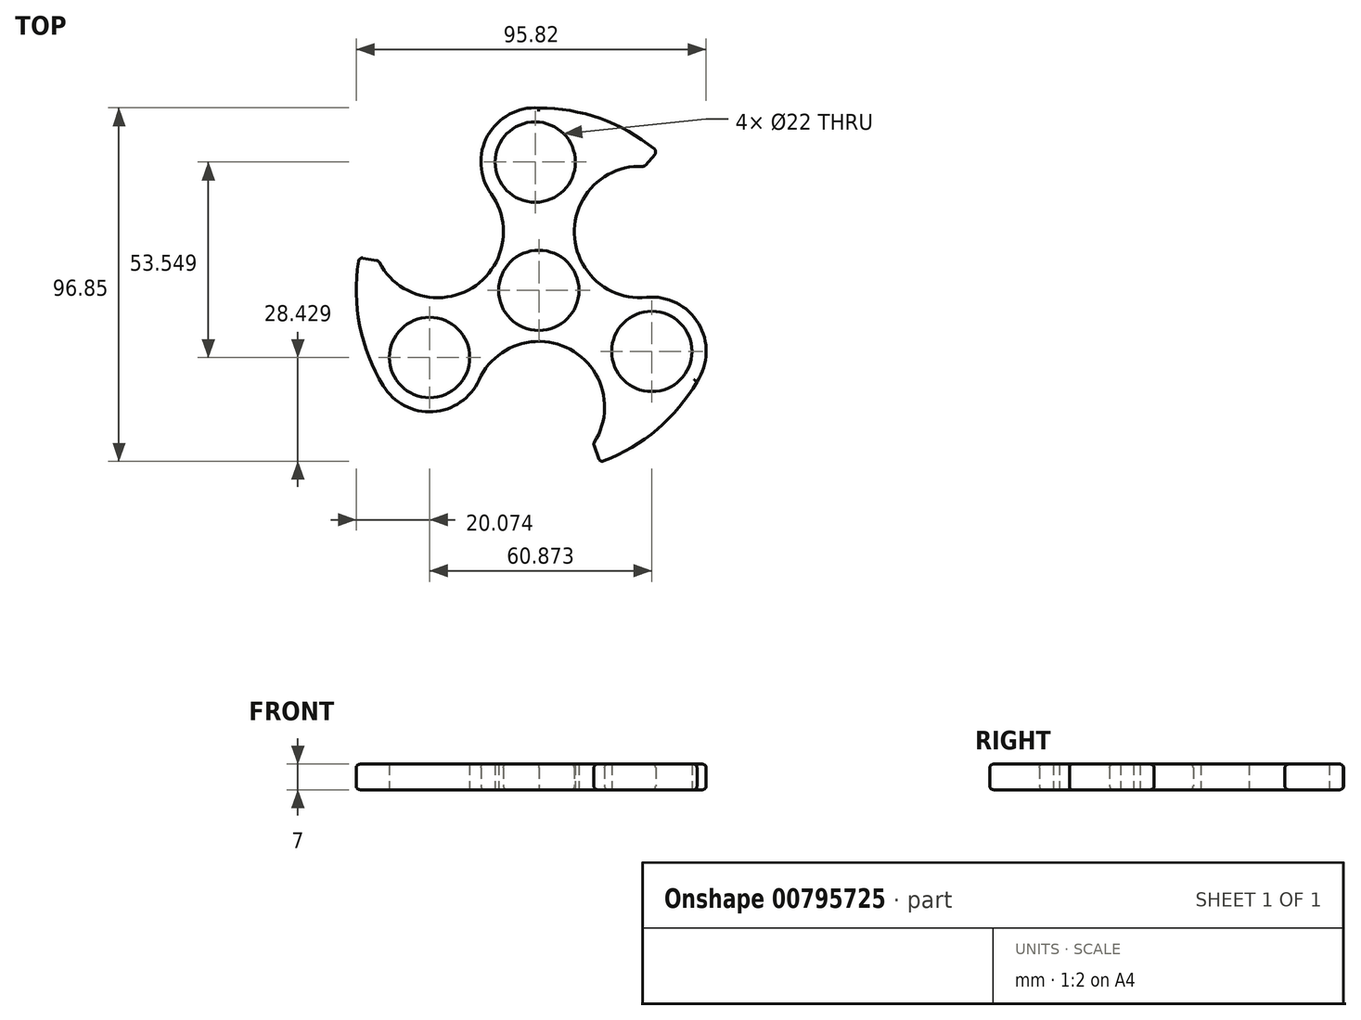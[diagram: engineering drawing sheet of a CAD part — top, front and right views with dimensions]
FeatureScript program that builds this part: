
annotation { "Feature Type Name" : "Feature", "Feature Type Description" : "" }
export const myFeature = defineFeature(function(context is Context, id is Id, definition is map)
    precondition{}
    {
        {
            var Q0;
            Q0=qCreatedBy(makeId("Top.planeOp"),FACE);
            var sketch = newSketch(context, id + "F0", { "sketchPlane" : qUnion([Q0])});
            skCircle(sketch, "E0", {"center": v(0, 0) * mm, "radius": 11 * mm});
            skArc(sketch, "E1", {"start": v(-49.18, 9.03) * mm, "mid": v(-49.15, -9.18) * mm, "end": v(-42.6, -26.18) * mm});
            skArc(sketch, "E2", {"start": v(-43.87, 8.06) * mm, "mid": v(-18.47, 0.56) * mm, "end": v(-13.09, 26.49) * mm});
            skArc(sketch, "E3", {"start": v(28.91, 33.96) * mm, "mid": v(9.72, 15.71) * mm, "end": v(29.48, -1.91) * mm});
            skArc(sketch, "E4", {"start": v(14.95, -42.02) * mm, "mid": v(8.77, -16.28) * mm, "end": v(-16.38, -24.53) * mm});
            skArc(sketch, "E5.trimOffspring", {"start": v(16.76, -47.1) * mm, "mid": v(32, -38.42) * mm, "end": v(43.3, -25) * mm});
            skArc(sketch, "E6.trimOffspring", {"start": v(32.41, 38.07) * mm, "mid": v(17.27, 46.92) * mm, "end": v(0, 50) * mm});
            skPoint(sketch, "E7", {"position": v(23.2, 38.55) * mm});
            skPoint(sketch, "E8", {"position": v(21.79, -39.38) * mm});
            skPoint(sketch, "E9", {"position": v(-45, 0.82) * mm});
            skArc(sketch, "E10", {"start": v(-13.09, 26.49) * mm, "mid": v(-14, 42.4) * mm, "end": v(0, 50) * mm});
            skArc(sketch, "E11", {"start": v(-42.6, -26.18) * mm, "mid": v(-29, -33.24) * mm, "end": v(-16.38, -24.53) * mm});
            skArc(sketch, "E12", {"start": v(29.48, -1.91) * mm, "mid": v(43.71, -9.08) * mm, "end": v(43.3, -25) * mm});
            skCircle(sketch, "E13", {"center": v(-29.93, -18.4) * mm, "radius": 11 * mm});
            skCircle(sketch, "E14", {"center": v(-1, 35.16) * mm, "radius": 11 * mm});
            skCircle(sketch, "E15", {"center": v(30.95, -16.72) * mm, "radius": 11 * mm});
            skLineSegment(sketch, "E16", {"start": v(0, 0) * mm, "end": v(37.87, 44.49) * mm, "construction": true});
            skLineSegment(sketch, "E17.1.0", {"start": v(0, 0) * mm, "end": v(-57.46, 10.56) * mm, "construction": true});
            skLineSegment(sketch, "E17.2.0", {"start": v(0, 0) * mm, "end": v(19.59, -55.04) * mm, "construction": true});
            skLineSegment(sketch, "E18", {"start": v(-49.18, 9.03) * mm, "end": v(-43.87, 8.06) * mm});
            skLineSegment(sketch, "E19", {"start": v(14.95, -42.02) * mm, "end": v(16.76, -47.1) * mm});
            skLineSegment(sketch, "E20", {"start": v(32.41, 38.07) * mm, "end": v(28.91, 33.96) * mm});
            skSolve(sketch);
        }
        {
            var Q0;
            {var subQ1=sQuery(id+"F0.wireOp",EDGE,"3f7bc842-8467-49ac-8440-9adaad4e2810.2");Q0=makeQuery(id+"F0.imprint","IMPRINT",FACE,{"disambiguationData":[TD([[makeQuery(id+"F0.imprint","IMPRINT",EDGE,{"derivedFrom":subQ1}),1.0]])]});}
            var Q1;
            {var subQ5=sQuery(id+"F0.wireOp",EDGE,"3f7bc842-8467-49ac-8440-9adaad4e2810.0");Q1=makeQuery(id+"F0.imprint","IMPRINT",FACE,{"disambiguationData":[TD([[makeQuery(id+"F0.imprint","IMPRINT",EDGE,{"derivedFrom":subQ5}),1.0]])]});}
            var Q2;
            {var subQ0=sQuery(id+"F0.wireOp",EDGE,"3f7bc842-8467-49ac-8440-9adaad4e2810.1");var subQ1=sQuery(id+"F0.wireOp",EDGE,"nu7MbhjY-MAc7-rPjX-g1DX-lD3kLk05fhsn");var subQ2=makeQuery(id+"F0.imprint","INTERSECT",VERTEX,{"derivedFrom":[subQ1,subQ0]});Q2=makeQuery(id+"F0.imprint","IMPRINT",FACE,{"disambiguationData":[TD([[makeQuery(id+"F0.imprint","IMPRINT",EDGE,{"disambiguationData":[TD([[subQ2,1.0]])],"derivedFrom":subQ0}),1.0]])]});}
            var Q3;
            {var subQ0=sQuery(id+"F0.wireOp",EDGE,"3f7bc842-8467-49ac-8440-9adaad4e2810.1");var subQ1=sQuery(id+"F0.wireOp",EDGE,"nu7MbhjY-MAc7-rPjX-g1DX-lD3kLk05fhsn");var subQ2=makeQuery(id+"F0.imprint","INTERSECT",VERTEX,{"derivedFrom":[subQ1,subQ0]});Q3=makeQuery(id+"F0.imprint","IMPRINT",FACE,{"disambiguationData":[TD([[makeQuery(id+"F0.imprint","IMPRINT",EDGE,{"disambiguationData":[TD([[subQ2,-1.0]])],"derivedFrom":subQ0}),1.0]])]});}
            var Q4;
            {var subQ0=sQuery(id+"F0.wireOp",EDGE,"E2");var subQ1=sQuery(id+"F0.wireOp",EDGE,"sv7fbsnc-qcye-DYNE-iSqw-857IQjWxAevf");var subQ2=makeQuery(id+"F0.imprint","INTERSECT",VERTEX,{"derivedFrom":[subQ1,subQ0]});Q4=makeQuery(id+"F0.imprint","IMPRINT",FACE,{"disambiguationData":[TD([[makeQuery(id+"F0.imprint","IMPRINT",EDGE,{"disambiguationData":[TD([[subQ2,-1.0]])],"derivedFrom":subQ1}),-1.0]])]});}
            var Q5;
            {var subQ0=sQuery(id+"F0.wireOp",EDGE,"E3");var subQ1=sQuery(id+"F0.wireOp",EDGE,"sv7fbsnc-qcye-DYNE-iSqw-857IQjWxAevf");var subQ2=makeQuery(id+"F0.imprint","INTERSECT",VERTEX,{"derivedFrom":[subQ1,subQ0]});Q5=makeQuery(id+"F0.imprint","IMPRINT",FACE,{"disambiguationData":[TD([[makeQuery(id+"F0.imprint","IMPRINT",EDGE,{"disambiguationData":[TD([[subQ2,1.0]])],"derivedFrom":subQ1}),-1.0]])]});}
            var Q6;
            {var subQ3=sQuery(id+"F0.wireOp",EDGE,"E2");var subQ5=sQuery(id+"F0.wireOp",EDGE,"C4j8nSnC-YMSu-Lszk-EYxg-b8w5SDZCJpY5");var subQ6=makeQuery(id+"F0.imprint","INTERSECT",VERTEX,{"disambiguationData":[OD(0.0)],"derivedFrom":[subQ5,subQ3]});Q6=makeQuery(id+"F0.imprint","IMPRINT",FACE,{"disambiguationData":[TD([[makeQuery(id+"F0.imprint","IMPRINT",EDGE,{"disambiguationData":[TD([[subQ6,1.0]])],"derivedFrom":subQ5}),1.0]])]});}
            var Q7;
            {var subQ1=sQuery(id+"F0.wireOp",EDGE,"C4j8nSnC-YMSu-Lszk-EYxg-b8w5SDZCJpY5");var subQ7=sQuery(id+"F0.wireOp",EDGE,"E3");var subQ9=makeQuery(id+"F0.imprint","INTERSECT",VERTEX,{"disambiguationData":[OD(1.0)],"derivedFrom":[subQ1,subQ7]});Q7=makeQuery(id+"F0.imprint","IMPRINT",FACE,{"disambiguationData":[TD([[makeQuery(id+"F0.imprint","IMPRINT",EDGE,{"disambiguationData":[TD([[subQ9,-1.0]])],"derivedFrom":subQ1}),1.0]])]});}
            var Q8;
            {var subQ1=sQuery(id+"F0.wireOp",EDGE,"C4j8nSnC-YMSu-Lszk-EYxg-b8w5SDZCJpY5");var subQ5=sQuery(id+"F0.wireOp",EDGE,"E2");var subQ6=makeQuery(id+"F0.imprint","INTERSECT",VERTEX,{"disambiguationData":[OD(1.0)],"derivedFrom":[subQ1,subQ5]});Q8=makeQuery(id+"F0.imprint","IMPRINT",FACE,{"disambiguationData":[TD([[makeQuery(id+"F0.imprint","IMPRINT",EDGE,{"disambiguationData":[TD([[subQ6,-1.0]])],"derivedFrom":subQ1}),1.0]])]});}
            var Q9;
            {var subQ1=sQuery(id+"F0.wireOp",EDGE,"C4j8nSnC-YMSu-Lszk-EYxg-b8w5SDZCJpY5");var subQ5=sQuery(id+"F0.wireOp",EDGE,"E4");var subQ6=makeQuery(id+"F0.imprint","INTERSECT",VERTEX,{"disambiguationData":[OD(0.0)],"derivedFrom":[subQ1,subQ5]});Q9=makeQuery(id+"F0.imprint","IMPRINT",FACE,{"disambiguationData":[TD([[makeQuery(id+"F0.imprint","IMPRINT",EDGE,{"disambiguationData":[TD([[subQ6,1.0]])],"derivedFrom":subQ1}),1.0]])]});}
            var Q10;
            {var subQ5=sQuery(id+"F0.wireOp",EDGE,"9VgUR1kC-HbJB-ABtG-h0EX-FUHrEpssJFZg");var subQ6=sQuery(id+"F0.wireOp",EDGE,"E0");var subQ7=makeQuery(id+"F0.imprint","INTERSECT",VERTEX,{"derivedFrom":[subQ6,subQ5]});Q10=makeQuery(id+"F0.imprint","IMPRINT",FACE,{"disambiguationData":[TD([[makeQuery(id+"F0.imprint","IMPRINT",EDGE,{"disambiguationData":[TD([[subQ7,-1.0]])],"derivedFrom":subQ6}),-1.0]])]});}
            var Q11;
            {var subQ1=sQuery(id+"F0.wireOp",EDGE,"E0");var subQ9=sQuery(id+"F0.wireOp",EDGE,"CFaMabJv-BaBl-nt57-wO3A-6JOnLyDZJUd2");var subQ11=makeQuery(id+"F0.imprint","INTERSECT",VERTEX,{"derivedFrom":[subQ1,subQ9]});Q11=makeQuery(id+"F0.imprint","IMPRINT",FACE,{"disambiguationData":[TD([[makeQuery(id+"F0.imprint","IMPRINT",EDGE,{"disambiguationData":[TD([[subQ11,1.0]])],"derivedFrom":subQ1}),-1.0]])]});}
            var Q12;
            {var subQ0=sQuery(id+"F0.wireOp",EDGE,"E3");var subQ1=sQuery(id+"F0.wireOp",EDGE,"x40MpVTq-PCuQ-1TBw-DNN8-5xuqoy8G5yz2");var subQ2=makeQuery(id+"F0.imprint","INTERSECT",VERTEX,{"derivedFrom":[subQ1,subQ0]});Q12=makeQuery(id+"F0.imprint","IMPRINT",FACE,{"disambiguationData":[TD([[makeQuery(id+"F0.imprint","IMPRINT",EDGE,{"disambiguationData":[TD([[subQ2,-1.0]])],"derivedFrom":subQ1}),-1.0]])]});}
            var Q13;
            {var subQ0=sQuery(id+"F0.wireOp",EDGE,"E4");var subQ1=sQuery(id+"F0.wireOp",EDGE,"x40MpVTq-PCuQ-1TBw-DNN8-5xuqoy8G5yz2");var subQ2=makeQuery(id+"F0.imprint","INTERSECT",VERTEX,{"derivedFrom":[subQ1,subQ0]});Q13=makeQuery(id+"F0.imprint","IMPRINT",FACE,{"disambiguationData":[TD([[makeQuery(id+"F0.imprint","IMPRINT",EDGE,{"disambiguationData":[TD([[subQ2,1.0]])],"derivedFrom":subQ1}),-1.0]])]});}
            var Q14;
            {var subQ0=sQuery(id+"F0.wireOp",EDGE,"49722dc7-dc7b-4ebf-b22a-0d9910023828.2");Q14=makeQuery(id+"F0.imprint","IMPRINT",FACE,{"disambiguationData":[TD([[makeQuery(id+"F0.imprint","IMPRINT",EDGE,{"derivedFrom":subQ0}),1.0]])]});}
            var Q15;
            {var subQ5=sQuery(id+"F0.wireOp",EDGE,"49722dc7-dc7b-4ebf-b22a-0d9910023828.0");Q15=makeQuery(id+"F0.imprint","IMPRINT",FACE,{"disambiguationData":[TD([[makeQuery(id+"F0.imprint","IMPRINT",EDGE,{"derivedFrom":subQ5}),1.0]])]});}
            var Q16;
            {var subQ0=sQuery(id+"F0.wireOp",EDGE,"E5.trimOffspring");Q16=makeQuery(id+"F0.imprint","IMPRINT",FACE,{"disambiguationData":[TD([[makeQuery(id+"F0.imprint","IMPRINT",EDGE,{"derivedFrom":subQ0}),1.0]])]});}
            var Q17;
            {var subQ0=sQuery(id+"F0.wireOp",EDGE,"49722dc7-dc7b-4ebf-b22a-0d9910023828.4");var subQ1=sQuery(id+"F0.wireOp",EDGE,"88UstpRX-54K3-uVYN-JsYc-c1O7LK7eOc8f");var subQ2=makeQuery(id+"F0.imprint","INTERSECT",VERTEX,{"derivedFrom":[subQ1,subQ0]});Q17=makeQuery(id+"F0.imprint","IMPRINT",FACE,{"disambiguationData":[TD([[makeQuery(id+"F0.imprint","IMPRINT",EDGE,{"disambiguationData":[TD([[subQ2,1.0]])],"derivedFrom":subQ0}),1.0]])]});}
            var Q18;
            {var subQ0=sQuery(id+"F0.wireOp",EDGE,"49722dc7-dc7b-4ebf-b22a-0d9910023828.4");var subQ1=sQuery(id+"F0.wireOp",EDGE,"88UstpRX-54K3-uVYN-JsYc-c1O7LK7eOc8f");var subQ2=makeQuery(id+"F0.imprint","INTERSECT",VERTEX,{"derivedFrom":[subQ1,subQ0]});Q18=makeQuery(id+"F0.imprint","IMPRINT",FACE,{"disambiguationData":[TD([[makeQuery(id+"F0.imprint","IMPRINT",EDGE,{"disambiguationData":[TD([[subQ2,-1.0]])],"derivedFrom":subQ0}),1.0]])]});}
            var Q19;
            {var subQ0=sQuery(id+"F0.wireOp",EDGE,"E6.trimOffspring");Q19=makeQuery(id+"F0.imprint","IMPRINT",FACE,{"disambiguationData":[TD([[makeQuery(id+"F0.imprint","IMPRINT",EDGE,{"derivedFrom":subQ0}),1.0]])]});}
            var Q20;
            {var subQ0=sQuery(id+"F0.wireOp",EDGE,"4Rxz6dJ8-GsAv-ijvN-txGC-AziJ4LwzvlZd");var subQ1=sQuery(id+"F0.wireOp",EDGE,"sv7fbsnc-qcye-DYNE-iSqw-857IQjWxAevf");var subQ2=makeQuery(id+"F0.imprint","INTERSECT",VERTEX,{"disambiguationData":[OD(0.0)],"derivedFrom":[subQ1,subQ0]});Q20=makeQuery(id+"F0.imprint","IMPRINT",FACE,{"disambiguationData":[TD([[makeQuery(id+"F0.imprint","IMPRINT",EDGE,{"disambiguationData":[TD([[subQ2,-1.0]])],"derivedFrom":subQ0}),1.0]])]});}
            var Q21;
            {var subQ0=sQuery(id+"F0.wireOp",EDGE,"4Rxz6dJ8-GsAv-ijvN-txGC-AziJ4LwzvlZd");var subQ1=sQuery(id+"F0.wireOp",EDGE,"sv7fbsnc-qcye-DYNE-iSqw-857IQjWxAevf");var subQ2=makeQuery(id+"F0.imprint","INTERSECT",VERTEX,{"disambiguationData":[OD(1.0)],"derivedFrom":[subQ1,subQ0]});Q21=makeQuery(id+"F0.imprint","IMPRINT",FACE,{"disambiguationData":[TD([[makeQuery(id+"F0.imprint","IMPRINT",EDGE,{"disambiguationData":[TD([[subQ2,1.0]])],"derivedFrom":subQ0}),1.0]])]});}
            var Q22;
            {var subQ0=sQuery(id+"F0.wireOp",EDGE,"4Rxz6dJ8-GsAv-ijvN-txGC-AziJ4LwzvlZd");var subQ3=sQuery(id+"F0.wireOp",EDGE,"C4j8nSnC-YMSu-Lszk-EYxg-b8w5SDZCJpY5");var subQ5=makeQuery(id+"F0.imprint","INTERSECT",VERTEX,{"disambiguationData":[OD(0.0)],"derivedFrom":[subQ3,subQ0]});Q22=makeQuery(id+"F0.imprint","IMPRINT",FACE,{"disambiguationData":[TD([[makeQuery(id+"F0.imprint","IMPRINT",EDGE,{"disambiguationData":[TD([[subQ5,-1.0]])],"derivedFrom":subQ3}),1.0]])]});}
            var Q23;
            {var subQ0=sQuery(id+"F0.wireOp",EDGE,"4Rxz6dJ8-GsAv-ijvN-txGC-AziJ4LwzvlZd");var subQ3=sQuery(id+"F0.wireOp",EDGE,"C4j8nSnC-YMSu-Lszk-EYxg-b8w5SDZCJpY5");var subQ5=makeQuery(id+"F0.imprint","INTERSECT",VERTEX,{"disambiguationData":[OD(1.0)],"derivedFrom":[subQ3,subQ0]});Q23=makeQuery(id+"F0.imprint","IMPRINT",FACE,{"disambiguationData":[TD([[makeQuery(id+"F0.imprint","IMPRINT",EDGE,{"disambiguationData":[TD([[subQ5,1.0]])],"derivedFrom":subQ3}),1.0]])]});}
            var Q24;
            {var subQ0=sQuery(id+"F0.wireOp",EDGE,"gMAYUmRH-FaYY-2lfT-oHka-ojM136KSUSHD");var subQ1=sQuery(id+"F0.wireOp",EDGE,"88UstpRX-54K3-uVYN-JsYc-c1O7LK7eOc8f");var subQ2=makeQuery(id+"F0.imprint","INTERSECT",VERTEX,{"disambiguationData":[OD(0.0)],"derivedFrom":[subQ1,subQ0]});Q24=makeQuery(id+"F0.imprint","IMPRINT",FACE,{"disambiguationData":[TD([[makeQuery(id+"F0.imprint","IMPRINT",EDGE,{"disambiguationData":[TD([[subQ2,-1.0]])],"derivedFrom":subQ1}),1.0]])]});}
            var Q25;
            {var subQ0=sQuery(id+"F0.wireOp",EDGE,"gMAYUmRH-FaYY-2lfT-oHka-ojM136KSUSHD");var subQ1=sQuery(id+"F0.wireOp",EDGE,"88UstpRX-54K3-uVYN-JsYc-c1O7LK7eOc8f");var subQ2=makeQuery(id+"F0.imprint","INTERSECT",VERTEX,{"disambiguationData":[OD(0.0)],"derivedFrom":[subQ1,subQ0]});Q25=makeQuery(id+"F0.imprint","IMPRINT",FACE,{"disambiguationData":[TD([[makeQuery(id+"F0.imprint","IMPRINT",EDGE,{"disambiguationData":[TD([[subQ2,-1.0]])],"derivedFrom":subQ1}),-1.0]])]});}
            var Q26;
            {var subQ1=sQuery(id+"F0.wireOp",EDGE,"88UstpRX-54K3-uVYN-JsYc-c1O7LK7eOc8f");var subQ5=sQuery(id+"F0.wireOp",EDGE,"C4j8nSnC-YMSu-Lszk-EYxg-b8w5SDZCJpY5");var subQ6=makeQuery(id+"F0.imprint","INTERSECT",VERTEX,{"derivedFrom":[subQ1,subQ5]});Q26=makeQuery(id+"F0.imprint","IMPRINT",FACE,{"disambiguationData":[TD([[makeQuery(id+"F0.imprint","IMPRINT",EDGE,{"disambiguationData":[TD([[subQ6,-1.0]])],"derivedFrom":subQ1}),-1.0]])]});}
            var Q27;
            {var subQ1=sQuery(id+"F0.wireOp",EDGE,"88UstpRX-54K3-uVYN-JsYc-c1O7LK7eOc8f");var subQ7=sQuery(id+"F0.wireOp",EDGE,"C4j8nSnC-YMSu-Lszk-EYxg-b8w5SDZCJpY5");var subQ8=makeQuery(id+"F0.imprint","INTERSECT",VERTEX,{"derivedFrom":[subQ1,subQ7]});Q27=makeQuery(id+"F0.imprint","IMPRINT",FACE,{"disambiguationData":[TD([[makeQuery(id+"F0.imprint","IMPRINT",EDGE,{"disambiguationData":[TD([[subQ8,-1.0]])],"derivedFrom":subQ1}),1.0]])]});}
            var Q28;
            {var subQ0=sQuery(id+"F0.wireOp",EDGE,"E1");Q28=makeQuery(id+"F0.imprint","IMPRINT",FACE,{"disambiguationData":[TD([[makeQuery(id+"F0.imprint","IMPRINT",EDGE,{"derivedFrom":subQ0}),1.0]])]});}
            var Q29;
            {var subQ1=sQuery(id+"F0.wireOp",EDGE,"d8093a5b-4d6d-4e08-b9a8-8a5bac8dbfa5.3");Q29=makeQuery(id+"F0.imprint","IMPRINT",FACE,{"disambiguationData":[TD([[makeQuery(id+"F0.imprint","IMPRINT",EDGE,{"derivedFrom":subQ1}),1.0]])]});}
            var Q30;
            {var subQ4=sQuery(id+"F0.wireOp",EDGE,"d8093a5b-4d6d-4e08-b9a8-8a5bac8dbfa5.0");Q30=makeQuery(id+"F0.imprint","IMPRINT",FACE,{"disambiguationData":[TD([[makeQuery(id+"F0.imprint","IMPRINT",EDGE,{"derivedFrom":subQ4}),1.0]])]});}
            var Q31;
            {var subQ0=sQuery(id+"F0.wireOp",EDGE,"E4");var subQ1=sQuery(id+"F0.wireOp",EDGE,"RUABtInU-iKBV-EQpS-h9ne-nRwwB5inRPBh");var subQ2=makeQuery(id+"F0.imprint","INTERSECT",VERTEX,{"derivedFrom":[subQ1,subQ0]});Q31=makeQuery(id+"F0.imprint","IMPRINT",FACE,{"disambiguationData":[TD([[makeQuery(id+"F0.imprint","IMPRINT",EDGE,{"disambiguationData":[TD([[subQ2,-1.0]])],"derivedFrom":subQ1}),-1.0]])]});}
            var Q32;
            {var subQ0=sQuery(id+"F0.wireOp",EDGE,"E2");var subQ1=sQuery(id+"F0.wireOp",EDGE,"RUABtInU-iKBV-EQpS-h9ne-nRwwB5inRPBh");var subQ2=makeQuery(id+"F0.imprint","INTERSECT",VERTEX,{"derivedFrom":[subQ1,subQ0]});Q32=makeQuery(id+"F0.imprint","IMPRINT",FACE,{"disambiguationData":[TD([[makeQuery(id+"F0.imprint","IMPRINT",EDGE,{"disambiguationData":[TD([[subQ2,1.0]])],"derivedFrom":subQ1}),-1.0]])]});}
            var Q33;
            {var subQ0=sQuery(id+"F0.wireOp",EDGE,"d8093a5b-4d6d-4e08-b9a8-8a5bac8dbfa5.5");var subQ1=sQuery(id+"F0.wireOp",EDGE,"mKOXe6AH-uMiB-TUgd-KZ6j-uo9zpwvRpa4S");var subQ2=makeQuery(id+"F0.imprint","INTERSECT",VERTEX,{"derivedFrom":[subQ1,subQ0]});Q33=makeQuery(id+"F0.imprint","IMPRINT",FACE,{"disambiguationData":[TD([[makeQuery(id+"F0.imprint","IMPRINT",EDGE,{"disambiguationData":[TD([[subQ2,-1.0]])],"derivedFrom":subQ0}),1.0]])]});}
            var Q34;
            {var subQ0=sQuery(id+"F0.wireOp",EDGE,"d8093a5b-4d6d-4e08-b9a8-8a5bac8dbfa5.5");var subQ1=sQuery(id+"F0.wireOp",EDGE,"mKOXe6AH-uMiB-TUgd-KZ6j-uo9zpwvRpa4S");var subQ2=makeQuery(id+"F0.imprint","INTERSECT",VERTEX,{"derivedFrom":[subQ1,subQ0]});Q34=makeQuery(id+"F0.imprint","IMPRINT",FACE,{"disambiguationData":[TD([[makeQuery(id+"F0.imprint","IMPRINT",EDGE,{"disambiguationData":[TD([[subQ2,1.0]])],"derivedFrom":subQ0}),1.0]])]});}
            var Q35;
            {var subQ0=sQuery(id+"F0.wireOp",EDGE,"kEFfzBxr-I8kb-SGwx-hxRS-iwMc0eVOOg4E");var subQ1=sQuery(id+"F0.wireOp",EDGE,"RUABtInU-iKBV-EQpS-h9ne-nRwwB5inRPBh");var subQ2=makeQuery(id+"F0.imprint","INTERSECT",VERTEX,{"disambiguationData":[OD(1.0)],"derivedFrom":[subQ1,subQ0]});Q35=makeQuery(id+"F0.imprint","IMPRINT",FACE,{"disambiguationData":[TD([[makeQuery(id+"F0.imprint","IMPRINT",EDGE,{"disambiguationData":[TD([[subQ2,1.0]])],"derivedFrom":subQ0}),1.0]])]});}
            var Q36;
            {var subQ0=sQuery(id+"F0.wireOp",EDGE,"kEFfzBxr-I8kb-SGwx-hxRS-iwMc0eVOOg4E");var subQ1=sQuery(id+"F0.wireOp",EDGE,"RUABtInU-iKBV-EQpS-h9ne-nRwwB5inRPBh");var subQ2=makeQuery(id+"F0.imprint","INTERSECT",VERTEX,{"disambiguationData":[OD(0.0)],"derivedFrom":[subQ1,subQ0]});Q36=makeQuery(id+"F0.imprint","IMPRINT",FACE,{"disambiguationData":[TD([[makeQuery(id+"F0.imprint","IMPRINT",EDGE,{"disambiguationData":[TD([[subQ2,-1.0]])],"derivedFrom":subQ0}),1.0]])]});}
            var Q37;
            {var subQ0=sQuery(id+"F0.wireOp",EDGE,"kEFfzBxr-I8kb-SGwx-hxRS-iwMc0eVOOg4E");var subQ3=sQuery(id+"F0.wireOp",EDGE,"C4j8nSnC-YMSu-Lszk-EYxg-b8w5SDZCJpY5");var subQ5=makeQuery(id+"F0.imprint","INTERSECT",VERTEX,{"disambiguationData":[OD(1.0)],"derivedFrom":[subQ3,subQ0]});Q37=makeQuery(id+"F0.imprint","IMPRINT",FACE,{"disambiguationData":[TD([[makeQuery(id+"F0.imprint","IMPRINT",EDGE,{"disambiguationData":[TD([[subQ5,1.0]])],"derivedFrom":subQ3}),1.0]])]});}
            var Q38;
            {var subQ0=sQuery(id+"F0.wireOp",EDGE,"kEFfzBxr-I8kb-SGwx-hxRS-iwMc0eVOOg4E");var subQ3=sQuery(id+"F0.wireOp",EDGE,"C4j8nSnC-YMSu-Lszk-EYxg-b8w5SDZCJpY5");var subQ5=makeQuery(id+"F0.imprint","INTERSECT",VERTEX,{"disambiguationData":[OD(0.0)],"derivedFrom":[subQ3,subQ0]});Q38=makeQuery(id+"F0.imprint","IMPRINT",FACE,{"disambiguationData":[TD([[makeQuery(id+"F0.imprint","IMPRINT",EDGE,{"disambiguationData":[TD([[subQ5,-1.0]])],"derivedFrom":subQ3}),1.0]])]});}
            var Q39;
            {var subQ0=sQuery(id+"F0.wireOp",EDGE,"DQ5kVecW-1MrT-lyVf-wv95-HuLgpyEHOht9");var subQ1=sQuery(id+"F0.wireOp",EDGE,"C4j8nSnC-YMSu-Lszk-EYxg-b8w5SDZCJpY5");var subQ2=makeQuery(id+"F0.imprint","INTERSECT",VERTEX,{"derivedFrom":[subQ1,subQ0]});Q39=makeQuery(id+"F0.imprint","IMPRINT",FACE,{"disambiguationData":[TD([[makeQuery(id+"F0.imprint","IMPRINT",EDGE,{"disambiguationData":[TD([[subQ2,-1.0]])],"derivedFrom":subQ1}),1.0]])]});}
            var Q40;
            {var subQ0=sQuery(id+"F0.wireOp",EDGE,"DQ5kVecW-1MrT-lyVf-wv95-HuLgpyEHOht9");var subQ1=sQuery(id+"F0.wireOp",EDGE,"C4j8nSnC-YMSu-Lszk-EYxg-b8w5SDZCJpY5");var subQ2=makeQuery(id+"F0.imprint","INTERSECT",VERTEX,{"derivedFrom":[subQ1,subQ0]});Q40=makeQuery(id+"F0.imprint","IMPRINT",FACE,{"disambiguationData":[TD([[makeQuery(id+"F0.imprint","IMPRINT",EDGE,{"disambiguationData":[TD([[subQ2,1.0]])],"derivedFrom":subQ1}),1.0]])]});}
            var Q41;
            {var subQ0=sQuery(id+"F0.wireOp",EDGE,"CFaMabJv-BaBl-nt57-wO3A-6JOnLyDZJUd2");var subQ1=sQuery(id+"F0.wireOp",EDGE,"C4j8nSnC-YMSu-Lszk-EYxg-b8w5SDZCJpY5");var subQ2=makeQuery(id+"F0.imprint","INTERSECT",VERTEX,{"derivedFrom":[subQ1,subQ0]});Q41=makeQuery(id+"F0.imprint","IMPRINT",FACE,{"disambiguationData":[TD([[makeQuery(id+"F0.imprint","IMPRINT",EDGE,{"disambiguationData":[TD([[subQ2,-1.0]])],"derivedFrom":subQ1}),1.0]])]});}
            var Q42;
            {var subQ0=sQuery(id+"F0.wireOp",EDGE,"CFaMabJv-BaBl-nt57-wO3A-6JOnLyDZJUd2");var subQ1=sQuery(id+"F0.wireOp",EDGE,"C4j8nSnC-YMSu-Lszk-EYxg-b8w5SDZCJpY5");var subQ2=makeQuery(id+"F0.imprint","INTERSECT",VERTEX,{"derivedFrom":[subQ1,subQ0]});Q42=makeQuery(id+"F0.imprint","IMPRINT",FACE,{"disambiguationData":[TD([[makeQuery(id+"F0.imprint","IMPRINT",EDGE,{"disambiguationData":[TD([[subQ2,1.0]])],"derivedFrom":subQ1}),1.0]])]});}
            var Q43;
            {var subQ0=sQuery(id+"F0.wireOp",EDGE,"9VgUR1kC-HbJB-ABtG-h0EX-FUHrEpssJFZg");var subQ1=sQuery(id+"F0.wireOp",EDGE,"C4j8nSnC-YMSu-Lszk-EYxg-b8w5SDZCJpY5");var subQ2=makeQuery(id+"F0.imprint","INTERSECT",VERTEX,{"derivedFrom":[subQ1,subQ0]});Q43=makeQuery(id+"F0.imprint","IMPRINT",FACE,{"disambiguationData":[TD([[makeQuery(id+"F0.imprint","IMPRINT",EDGE,{"disambiguationData":[TD([[subQ2,-1.0]])],"derivedFrom":subQ1}),1.0]])]});}
            var Q44;
            {var subQ0=sQuery(id+"F0.wireOp",EDGE,"9VgUR1kC-HbJB-ABtG-h0EX-FUHrEpssJFZg");var subQ1=sQuery(id+"F0.wireOp",EDGE,"C4j8nSnC-YMSu-Lszk-EYxg-b8w5SDZCJpY5");var subQ2=makeQuery(id+"F0.imprint","INTERSECT",VERTEX,{"derivedFrom":[subQ1,subQ0]});Q44=makeQuery(id+"F0.imprint","IMPRINT",FACE,{"disambiguationData":[TD([[makeQuery(id+"F0.imprint","IMPRINT",EDGE,{"disambiguationData":[TD([[subQ2,1.0]])],"derivedFrom":subQ1}),1.0]])]});}
            extrude(context, id + "F1", {"entities" : qUnion([Q0, Q1, Q2, Q3, Q4, Q5, Q6, Q7, Q8, Q9, Q10, Q11, Q12, Q13, Q14, Q15, Q16, Q17, Q18, Q19, Q20, Q21, Q22, Q23, Q24, Q25, Q26, Q27, Q28, Q29, Q30, Q31, Q32, Q33, Q34, Q35, Q36, Q37, Q38, Q39, Q40, Q41, Q42, Q43, Q44]), "depth" : 7 * mm, "offsetDistance" : 25 * mm});
        }
        {
            var Q0;
            Q0=makeQuery(id+"F1.opExtrude","CAP_EDGE",EDGE,{"disambiguationData":[OSD([sQuery(id+"F0.wireOp",EDGE,"E2")])],"isStart":false});
            var Q1;
            Q1=makeQuery(id+"F1.opExtrude","CAP_EDGE",EDGE,{"disambiguationData":[OSD([sQuery(id+"F0.wireOp",EDGE,"E4")])],"isStart":false});
            var Q2;
            Q2=makeQuery(id+"F1.opExtrude","CAP_EDGE",EDGE,{"disambiguationData":[OSD([sQuery(id+"F0.wireOp",EDGE,"E3")])],"isStart":false});
            var Q3;
            Q3=makeQuery(id+"F1.opExtrude","CAP_EDGE",EDGE,{"disambiguationData":[OSD([sQuery(id+"F0.wireOp",EDGE,"E10")])],"isStart":true});
            var Q4;
            Q4=makeQuery(id+"F1.opExtrude","CAP_EDGE",EDGE,{"disambiguationData":[OSD([sQuery(id+"F0.wireOp",EDGE,"E4")])],"isStart":true});
            var Q5;
            Q5=makeQuery(id+"F1.opExtrude","CAP_EDGE",EDGE,{"disambiguationData":[OSD([sQuery(id+"F0.wireOp",EDGE,"E5.trimOffspring")])],"isStart":true});
            var Q6;
            Q6=makeQuery(id+"F1.opExtrude","CAP_EDGE",EDGE,{"disambiguationData":[OSD([sQuery(id+"F0.wireOp",EDGE,"E18")])],"isStart":false});
            var Q7;
            Q7=makeQuery(id+"F1.opExtrude","CAP_EDGE",EDGE,{"disambiguationData":[OSD([sQuery(id+"F0.wireOp",EDGE,"E18")])],"isStart":true});
            var Q8;
            Q8=makeQuery(id+"F1.opExtrude","CAP_EDGE",EDGE,{"disambiguationData":[OSD([sQuery(id+"F0.wireOp",EDGE,"E19")])],"isStart":false});
            var Q9;
            Q9=makeQuery(id+"F1.opExtrude","CAP_EDGE",EDGE,{"disambiguationData":[OSD([sQuery(id+"F0.wireOp",EDGE,"E19")])],"isStart":true});
            var Q10;
            Q10=makeQuery(id+"F1.opExtrude","SWEPT_EDGE",EDGE,{"disambiguationData":[OSD([sQuery(id+"F0.wireOp",EDGE,"E4"),sQuery(id+"F0.wireOp",EDGE,"E19")])]});
            var Q11;
            Q11=makeQuery(id+"F1.opExtrude","SWEPT_EDGE",EDGE,{"disambiguationData":[OSD([sQuery(id+"F0.wireOp",EDGE,"E5.trimOffspring"),sQuery(id+"F0.wireOp",EDGE,"E19")])]});
            var Q12;
            Q12=makeQuery(id+"F1.opExtrude","SWEPT_EDGE",EDGE,{"disambiguationData":[OSD([sQuery(id+"F0.wireOp",EDGE,"E3"),sQuery(id+"F0.wireOp",EDGE,"E20")])]});
            var Q13;
            Q13=makeQuery(id+"F1.opExtrude","CAP_EDGE",EDGE,{"disambiguationData":[OSD([sQuery(id+"F0.wireOp",EDGE,"E20")])],"isStart":false});
            var Q14;
            Q14=makeQuery(id+"F1.opExtrude","SWEPT_EDGE",EDGE,{"disambiguationData":[OSD([sQuery(id+"F0.wireOp",EDGE,"E6.trimOffspring"),sQuery(id+"F0.wireOp",EDGE,"E20")])]});
            var Q15;
            Q15=makeQuery(id+"F1.opExtrude","CAP_EDGE",EDGE,{"disambiguationData":[OSD([sQuery(id+"F0.wireOp",EDGE,"E20")])],"isStart":true});
            var Q16;
            Q16=makeQuery(id+"F1.opExtrude","SWEPT_EDGE",EDGE,{"disambiguationData":[OSD([sQuery(id+"F0.wireOp",EDGE,"E2"),sQuery(id+"F0.wireOp",EDGE,"E18")])]});
            var Q17;
            Q17=makeQuery(id+"F1.opExtrude","SWEPT_EDGE",EDGE,{"disambiguationData":[OSD([sQuery(id+"F0.wireOp",EDGE,"E1"),sQuery(id+"F0.wireOp",EDGE,"E18")])]});
            var Q18;
            Q18=makeQuery(id+"F1.opExtrude","CAP_EDGE",EDGE,{"disambiguationData":[OSD([sQuery(id+"F0.wireOp",EDGE,"E1")])],"isStart":false});
            var Q19;
            Q19=makeQuery(id+"F1.opExtrude","CAP_EDGE",EDGE,{"disambiguationData":[OSD([sQuery(id+"F0.wireOp",EDGE,"E11")])],"isStart":false});
            var Q20;
            Q20=makeQuery(id+"F1.opExtrude","CAP_EDGE",EDGE,{"disambiguationData":[OSD([sQuery(id+"F0.wireOp",EDGE,"E11")])],"isStart":true});
            var Q21;
            Q21=makeQuery(id+"F1.opExtrude","CAP_EDGE",EDGE,{"disambiguationData":[OSD([sQuery(id+"F0.wireOp",EDGE,"E1")])],"isStart":true});
            var Q22;
            Q22=makeQuery(id+"F1.opExtrude","CAP_EDGE",EDGE,{"disambiguationData":[OSD([sQuery(id+"F0.wireOp",EDGE,"E12")])],"isStart":true});
            var Q23;
            Q23=makeQuery(id+"F1.opExtrude","CAP_EDGE",EDGE,{"disambiguationData":[OSD([sQuery(id+"F0.wireOp",EDGE,"E3")])],"isStart":true});
            var Q24;
            Q24=makeQuery(id+"F1.opExtrude","CAP_EDGE",EDGE,{"disambiguationData":[OSD([sQuery(id+"F0.wireOp",EDGE,"E6.trimOffspring")])],"isStart":true});
            fillet(context, id + "F2", {"entities" : qUnion([Q0, Q1, Q2, Q3, Q4, Q5, Q6, Q7, Q8, Q9, Q10, Q11, Q12, Q13, Q14, Q15, Q16, Q17, Q18, Q19, Q20, Q21, Q22, Q23, Q24]), "radius" : 1 * mm, "tangentPropagation" : true, "allowEdgeOverflow" : false});
        }
    });
